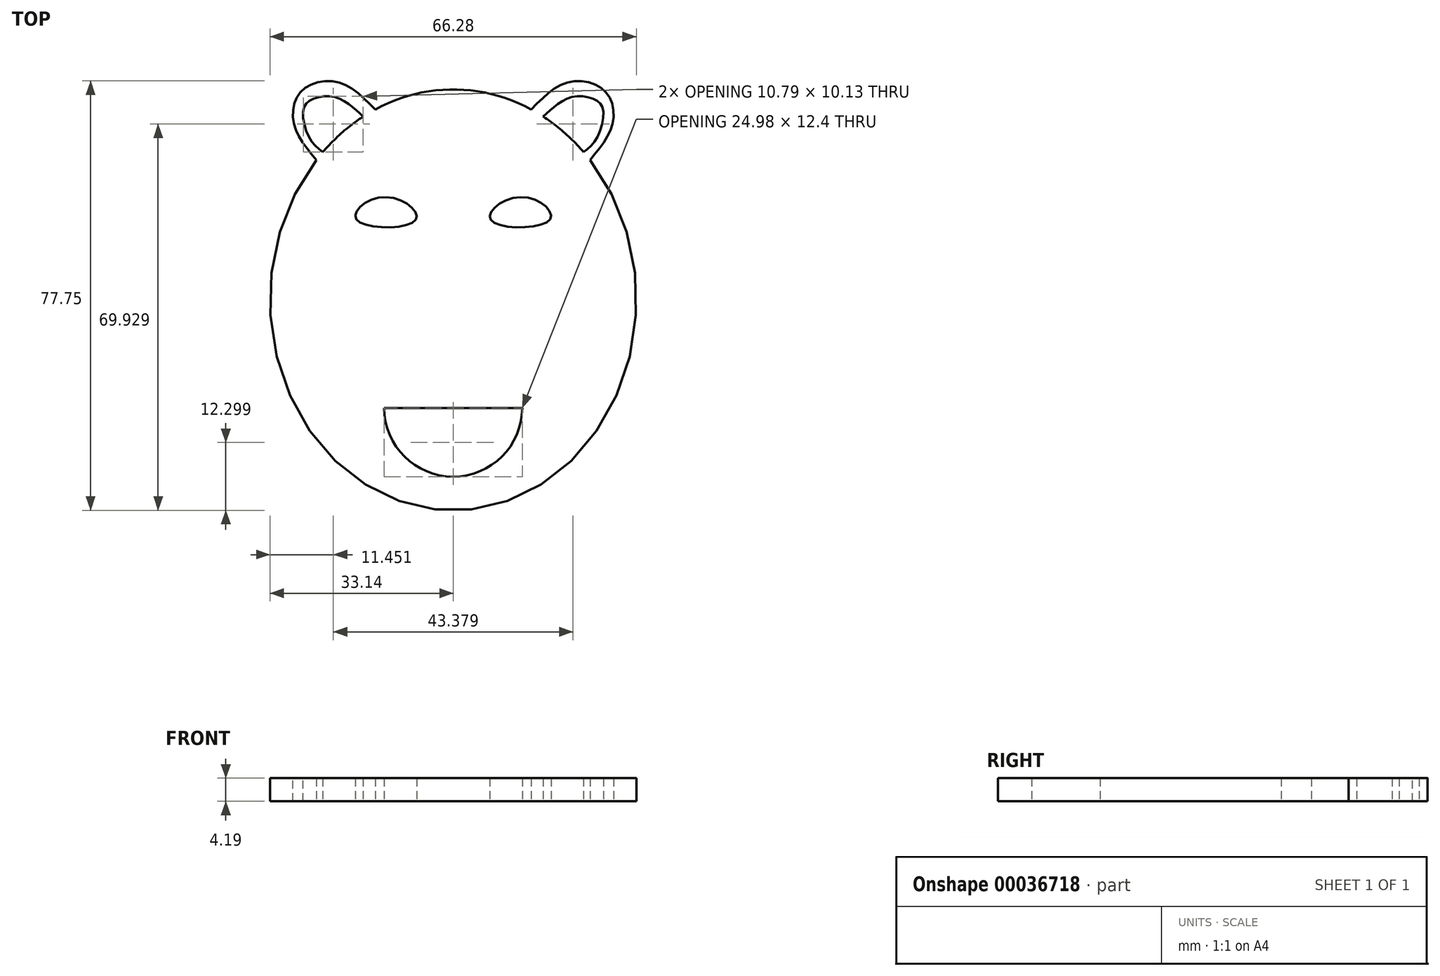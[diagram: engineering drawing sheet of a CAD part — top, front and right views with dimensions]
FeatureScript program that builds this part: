
annotation { "Feature Type Name" : "Feature", "Feature Type Description" : "" }
export const myFeature = defineFeature(function(context is Context, id is Id, definition is map)
    precondition{}
    {
        {
            var Q0;
            Q0=qCreatedBy(makeId("Top.planeOp"),FACE);
            var sketch = newSketch(context, id + "F0", { "sketchPlane" : qUnion([Q0])});
            skEllipticalArc(sketch, "E0", {});
            skFitSpline(sketch, "E1", {"points": [v(6.78, 14.5) * mm, v(12.38, 18.61) * mm, v(17.48, 14.54) * mm, v(6.78, 14.5) * mm]});
            skPoint(sketch, "E2.second.point", {"position": v(12.38, 13.14) * mm});
            skCircle(sketch, "E3", {"center": v(12.5, 15.87) * mm, "radius": 2.45 * mm});
            skLineSegment(sketch, "E4", {"start": v(0, 0) * mm, "end": v(0, 26.02) * mm, "construction": true});
            skFitSpline(sketch, "E5.MirrorC", {"points": [v(-6.78, 14.5) * mm, v(-12.38, 18.61) * mm, v(-17.48, 14.54) * mm, v(-6.78, 14.5) * mm]});
            skCircle(sketch, "E6.MirrorC", {"center": v(-12.5, 15.87) * mm, "radius": 2.45 * mm});
            skPoint(sketch, "E7", {"position": v(0, -19.6) * mm});
            skLineSegment(sketch, "E8", {"start": v(12.5, -19.6) * mm, "end": v(-12.5, -19.6) * mm});
            skArc(sketch, "E9", {"start": v(-12.5, -19.6) * mm, "mid": v(0, -32) * mm, "end": v(12.5, -19.6) * mm});
            skLineSegment(sketch, "E10", {"start": v(-10.4, 38.34) * mm, "end": v(-10.28, 38.1) * mm});
            skFitSpline(sketch, "E11.MirrorCS", {"points": [v(-24.75, 25.33) * mm, v(-28.8, 31.82) * mm, v(-27.49, 37.75) * mm, v(-20.94, 39.45) * mm, v(-14.12, 34.47) * mm], "startDerivative": vector(-20.27, 24.12) * mm, "endDerivative": vector(23.43, -24.22) * mm});
            skFitSpline(sketch, "E12.MirrorCS", {"points": [v(-16.3, 33.18) * mm, v(-18.62, 35.21) * mm, v(-21.94, 36.83) * mm, v(-25.56, 36.29) * mm, v(-27.11, 34.47) * mm, v(-26.02, 29.35) * mm, v(-23.59, 26.76) * mm], "startDerivative": vector(-14.15, 13.38) * mm, "endDerivative": vector(15.88, -12.35) * mm});
            skLineSegment(sketch, "E13", {"start": v(-23.59, 26.76) * mm, "end": v(-23.59, 26.77) * mm});
            skFitSpline(sketch, "E14.MirrorCS", {"points": [v(16.3, 33.18) * mm, v(18.62, 35.21) * mm, v(21.94, 36.83) * mm, v(25.56, 36.29) * mm, v(27.11, 34.47) * mm, v(26.02, 29.35) * mm, v(23.59, 26.76) * mm], "startDerivative": vector(14.15, 13.38) * mm, "endDerivative": vector(-15.88, -12.35) * mm});
            skFitSpline(sketch, "E15.MirrorCS", {"points": [v(24.75, 25.33) * mm, v(28.8, 31.82) * mm, v(27.49, 37.75) * mm, v(20.94, 39.45) * mm, v(14.12, 34.47) * mm], "startDerivative": vector(20.27, 24.12) * mm, "endDerivative": vector(-23.43, -24.22) * mm});
            skEllipticalArc(sketch, "E16.trimOffspring", {});
            skEllipticalArc(sketch, "E17.trimOffspring", {});
            skEllipticalArc(sketch, "E18.trimOffspring", {});
            const initialGuessF0  = {"E0": [0, 0, 0, -1, 0.0381, 0.03313956015813581, 2.7013414073294784, 3.581843899850107], "E16.trimOffspring": [0, 0, 0, -1, 0.0381, 0.03313956015813581, 3.6555446104390588, 3.9335228531496735], "E17.trimOffspring": [0, 0, 0, -1, 0.0381, 0.03313956015813581, 3.9850024641448365, 2.2981828430347484], "E18.trimOffspring": [0, 0, 0, -1, 0.0381, 0.03313956015813581, 2.3496624540299127, 2.6276406967405266]};
            skSetInitialGuess(sketch, initialGuessF0);
            skSolve(sketch);
        }
        {
            var Q0;
            Q0 = qSketchRegion(id + "F0", true);
            extrude(context, id + "F1", {"entities" : qUnion([Q0]), "depth" : 4.2 * mm});
        }
    });
